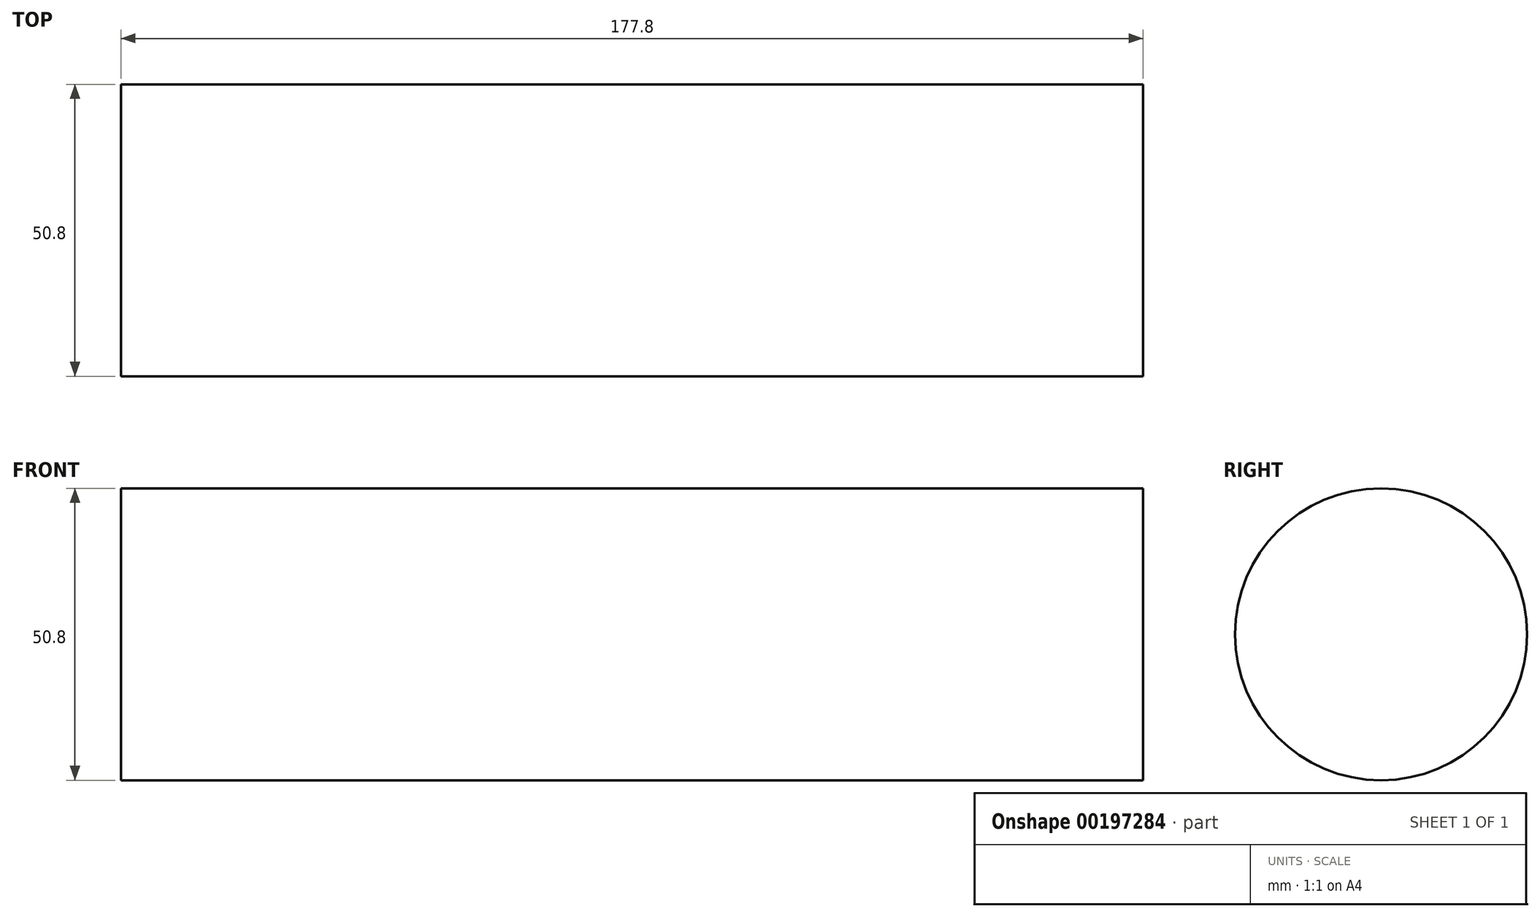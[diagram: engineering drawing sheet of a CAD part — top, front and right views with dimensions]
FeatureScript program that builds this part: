
annotation { "Feature Type Name" : "Feature", "Feature Type Description" : "" }
export const myFeature = defineFeature(function(context is Context, id is Id, definition is map)
    precondition{}
    {
        {
            var Q0;
            Q0=qCreatedBy(makeId("Right.planeOp"),FACE);
            var sketch = newSketch(context, id + "F0", { "sketchPlane" : qUnion([Q0])});
            skCircle(sketch, "E0", {"center": v(0, 0) * mm, "radius": 25.4 * mm});
            skSolve(sketch);
        }
        {
            var Q0;
            Q0=makeQuery(id+"F0.imprint","IMPRINT",FACE,{"disambiguationData":[TD([[makeQuery(id+"F0.imprint","IMPRINT",EDGE,{"derivedFrom":sQuery(id+"F0.wireOp",EDGE,"E0")}),1.0]])]});
            extrude(context, id + "F1", {"entities" : qUnion([Q0]), "depth" : 177.8 * mm});
        }
    });
